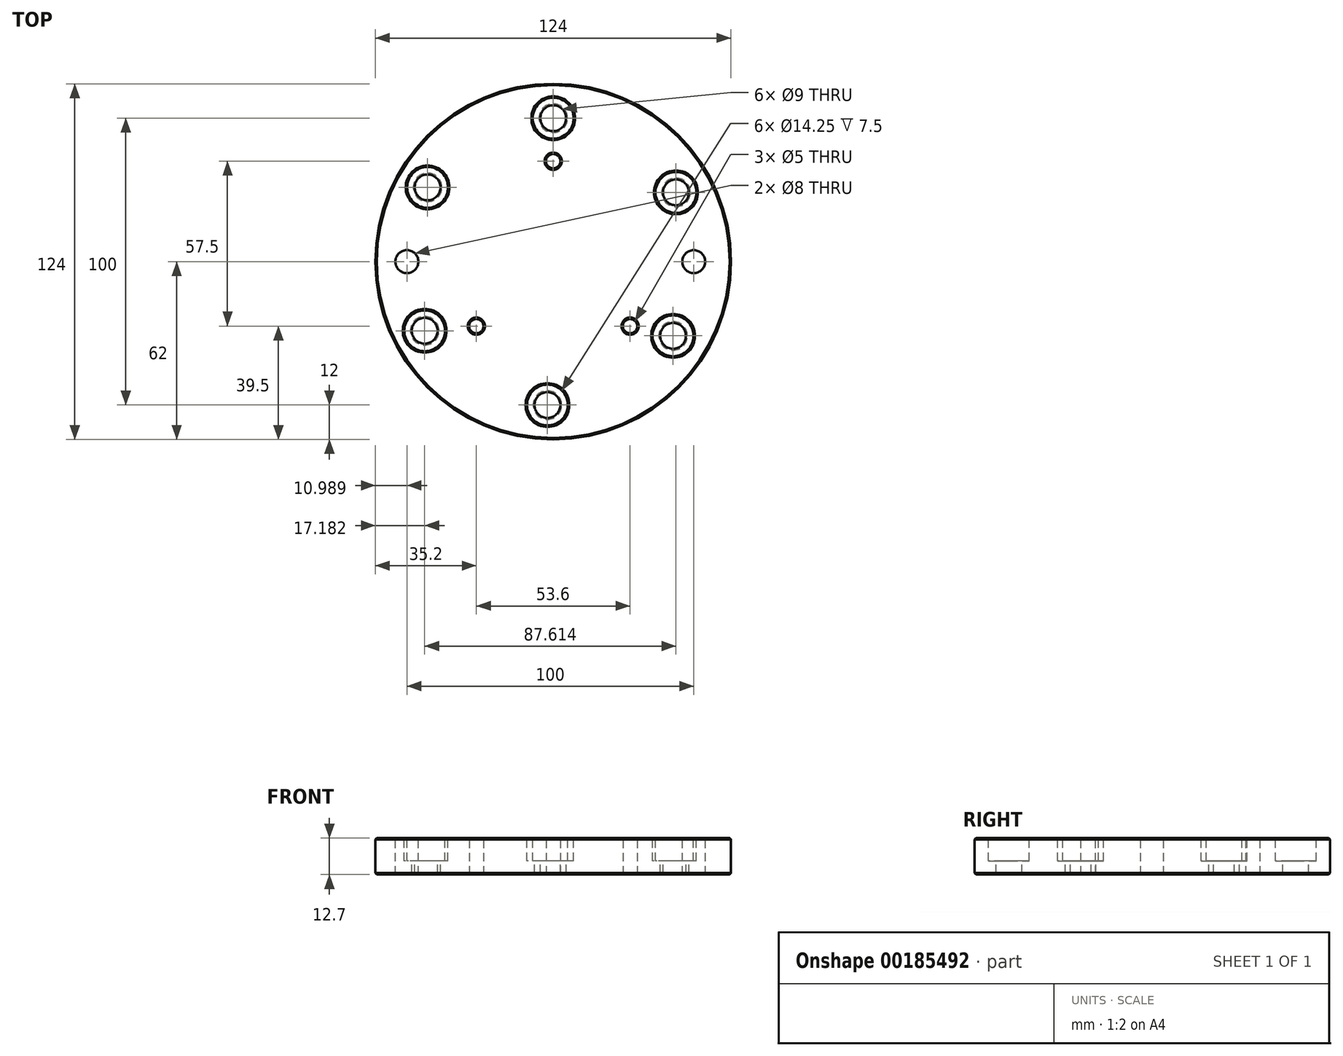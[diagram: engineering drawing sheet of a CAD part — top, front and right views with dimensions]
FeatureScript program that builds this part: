
annotation { "Feature Type Name" : "Feature", "Feature Type Description" : "" }
export const myFeature = defineFeature(function(context is Context, id is Id, definition is map)
    precondition{}
    {
        {
            var Q0;
            Q0=qCreatedBy(makeId("Top.planeOp"),FACE);
            var sketch = newSketch(context, id + "F0", { "sketchPlane" : qUnion([Q0])});
            skCircle(sketch, "E0", {"center": v(0, 0) * mm, "radius": 62 * mm});
            skPoint(sketch, "E1", {"position": v(0, 35) * mm});
            skPoint(sketch, "E2", {"position": v(-26.8, -22.5) * mm});
            skPoint(sketch, "E3", {"position": v(26.8, -22.5) * mm});
            skSolve(sketch);
        }
        {
            var Q0;
            Q0=makeQuery(id+"F0.imprint","IMPRINT",FACE,{"disambiguationData":[TD([[makeQuery(id+"F0.imprint","IMPRINT",EDGE,{"derivedFrom":sQuery(id+"F0.wireOp",EDGE,"E0")}),1.0]])]});
            extrude(context, id + "F1", {"entities" : qUnion([Q0]), "depth" : 12.7 * mm});
        }
        {
            var Q0;
            Q0=sQuery(id+"F0.wireOp",VERTEX,"41fbed7c-82ae-4e81-8245-005a1a350cab");
            var Q1;
            Q1=sQuery(id+"F0.wireOp",VERTEX,"E1");
            var Q2;
            Q2=sQuery(id+"F0.wireOp",VERTEX,"bce9c8f1-775d-439e-b54f-2bbc72c7738a");
            var Q3;
            Q3=sQuery(id+"F0.wireOp",VERTEX,"E3");
            var Q4;
            Q4=sQuery(id+"F0.wireOp",VERTEX,"E2");
            var Q5;
            Q5=makeQuery(id+"F1.opExtrude","SWEPT_BODY",BODY,{"disambiguationData":[OSD([sQuery(id+"F0.wireOp",EDGE,"E0")])]});
            hole(context, id + "F2", {"style" : HoleStyle.SIMPLE, "endStyle" : HoleEndStyle.THROUGH, "oppositeDirection" : true, "standardTappedOrClearance" : lookupTablePath({ "standard" : "ISO", "engagement" : "75%", "pitch" : "1 mm", "size" : "M6", "type" : "Tapped" }), "standardBlindInLast" : lookupTablePath({ "standard" : "ISO", "fit" : "Normal", "engagement" : "75%", "pitch" : "1 mm", "size" : "M6", "type" : "Clearance & tapped" }), "holeDiameter" : 5 * mm, "startFromSketch" : true, "locations" : qUnion([Q0, Q1, Q2, Q3, Q4]), "scope" : qUnion([Q5]), "isTappedThrough" : true, "tappedDepth" : 12 * mm, "tapClearance" : 3, "majorDiameter" : 6 * mm, "showTappedDepth" : true});
        }
        {
            var Q0;
            Q0=makeQuery(id+"F1.opExtrude","CAP_FACE",FACE,{"disambiguationData":[OSD([sQuery(id+"F0.wireOp",EDGE,"E0")])],"isStart":false});
            var sketch = newSketch(context, id + "F3", { "sketchPlane" : qUnion([Q0])});
            skPoint(sketch, "E4", {"position": v(0, 50) * mm});
            skPoint(sketch, "E5.1.0", {"position": v(-43.8, 25.88) * mm});
            skPoint(sketch, "E5.2.0", {"position": v(-44.82, -24.12) * mm});
            skPoint(sketch, "E5.3.0", {"position": v(-2.02, -50) * mm});
            skPoint(sketch, "E5.4.0", {"position": v(41.78, -25.88) * mm});
            skPoint(sketch, "E5.5.0", {"position": v(42.8, 24.12) * mm});
            skPoint(sketch, "E5.center", {"position": v(-1.01, 0) * mm});
            skPoint(sketch, "E6", {"position": v(-51.01, 0) * mm});
            skPoint(sketch, "E7", {"position": v(48.99, 0) * mm});
            skSolve(sketch);
        }
        {
            var Q0;
            Q0=sQuery(id+"F3.wireOp",VERTEX,"E4");
            var Q1;
            Q1=sQuery(id+"F3.wireOp",VERTEX,"E5.1.0");
            var Q2;
            Q2=sQuery(id+"F3.wireOp",VERTEX,"E5.5.0");
            var Q3;
            Q3=sQuery(id+"F3.wireOp",VERTEX,"E5.2.0");
            var Q4;
            Q4=sQuery(id+"F3.wireOp",VERTEX,"E5.3.0");
            var Q5;
            Q5=sQuery(id+"F3.wireOp",VERTEX,"E5.4.0");
            var Q6;
            Q6=makeQuery(id+"F1.opExtrude","SWEPT_BODY",BODY,{"disambiguationData":[OSD([sQuery(id+"F0.wireOp",EDGE,"E0")])]});
            hole(context, id + "F4", {"style" : HoleStyle.C_BORE, "endStyle" : HoleEndStyle.THROUGH, "standardTappedOrClearance" : lookupTablePath({ "fit" : "Normal", "standard" : "ISO", "size" : "M8", "type" : "Clearance" }), "standardBlindInLast" : lookupTablePath({ "fit" : "Normal", "standard" : "ISO", "engagement" : "75%", "pitch" : "1.25 mm", "size" : "M8", "type" : "Clearance & tapped" }), "holeDiameter" : 9 * mm, "cBoreDiameter" : 14.25 * mm, "cBoreDepth" : 8 * mm, "startFromSketch" : true, "locations" : qUnion([Q0, Q1, Q2, Q3, Q4, Q5]), "scope" : qUnion([Q6]), "isTappedThrough" : true, "tappedDepth" : 12 * mm, "tapClearance" : 3, "majorDiameter" : 6 * mm});
        }
        {
            var Q0;
            Q0=makeQuery(id+"F1.opExtrude","CAP_FACE",FACE,{"disambiguationData":[OSD([sQuery(id+"F0.wireOp",EDGE,"E0")])],"isStart":false});
            var Q1;
            Q1=makeQuery(id+"F1.opExtrude","CAP_FACE",FACE,{"disambiguationData":[OSD([sQuery(id+"F0.wireOp",EDGE,"E0")])],"isStart":true});
            chamfer(context, id + "F5", {"entities" : qUnion([Q0, Q1]), "width" : .5 * mm, "tangentPropagation" : true});
        }
        {
            var Q0;
            Q0=sQuery(id+"F3.wireOp",VERTEX,"E6");
            var Q1;
            Q1=sQuery(id+"F3.wireOp",VERTEX,"E7");
            var Q2;
            Q2=makeQuery(id+"F1.opExtrude","SWEPT_BODY",BODY,{"disambiguationData":[OSD([sQuery(id+"F0.wireOp",EDGE,"E0")])]});
            hole(context, id + "F6", {"style" : HoleStyle.SIMPLE, "endStyle" : HoleEndStyle.THROUGH, "standardTappedOrClearance" : lookupTablePath({ "standard" : "ISO", "size" : "8", "type" : "Drilled" }), "standardBlindInLast" : lookupTablePath({ "standard" : "ISO", "size" : "8", "type" : "Drilled" }), "holeDiameter" : 8 * mm, "majorDiameter" : 5 * mm, "isTappedThrough" : true, "tappedDepth" : 12 * mm, "tapClearance" : 3, "startFromSketch" : true, "locations" : qUnion([Q0, Q1]), "scope" : qUnion([Q2])});
        }
    });
